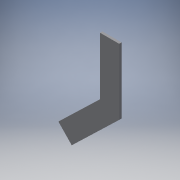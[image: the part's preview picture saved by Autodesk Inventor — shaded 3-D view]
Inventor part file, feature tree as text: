
AUTODESK INVENTOR PART (.ipt)
format: ipt  version: 2016 (Build 200138000, 138)  size: 92,672 bytes
history: native  units: in
note: dims shown in document units (in); Inventor stores cm internally (conversion verified against a paired STEP export)
features: extrude x1, sketch x1
ambient origin geometry x8: Origin, YZ Plane, XZ Plane, XY Plane, X Axis, Y Axis, Z Axis, Center Point
bodies: Solid1 (feature_tree)
feature tree (2):
  extrude  "Extrusion1"  Depth=0.125in
  sketch  "Sketch1"  dims[d0=1.0in d1=3.0in d2=0.9202in d3=0.125in d4=0.0in]
